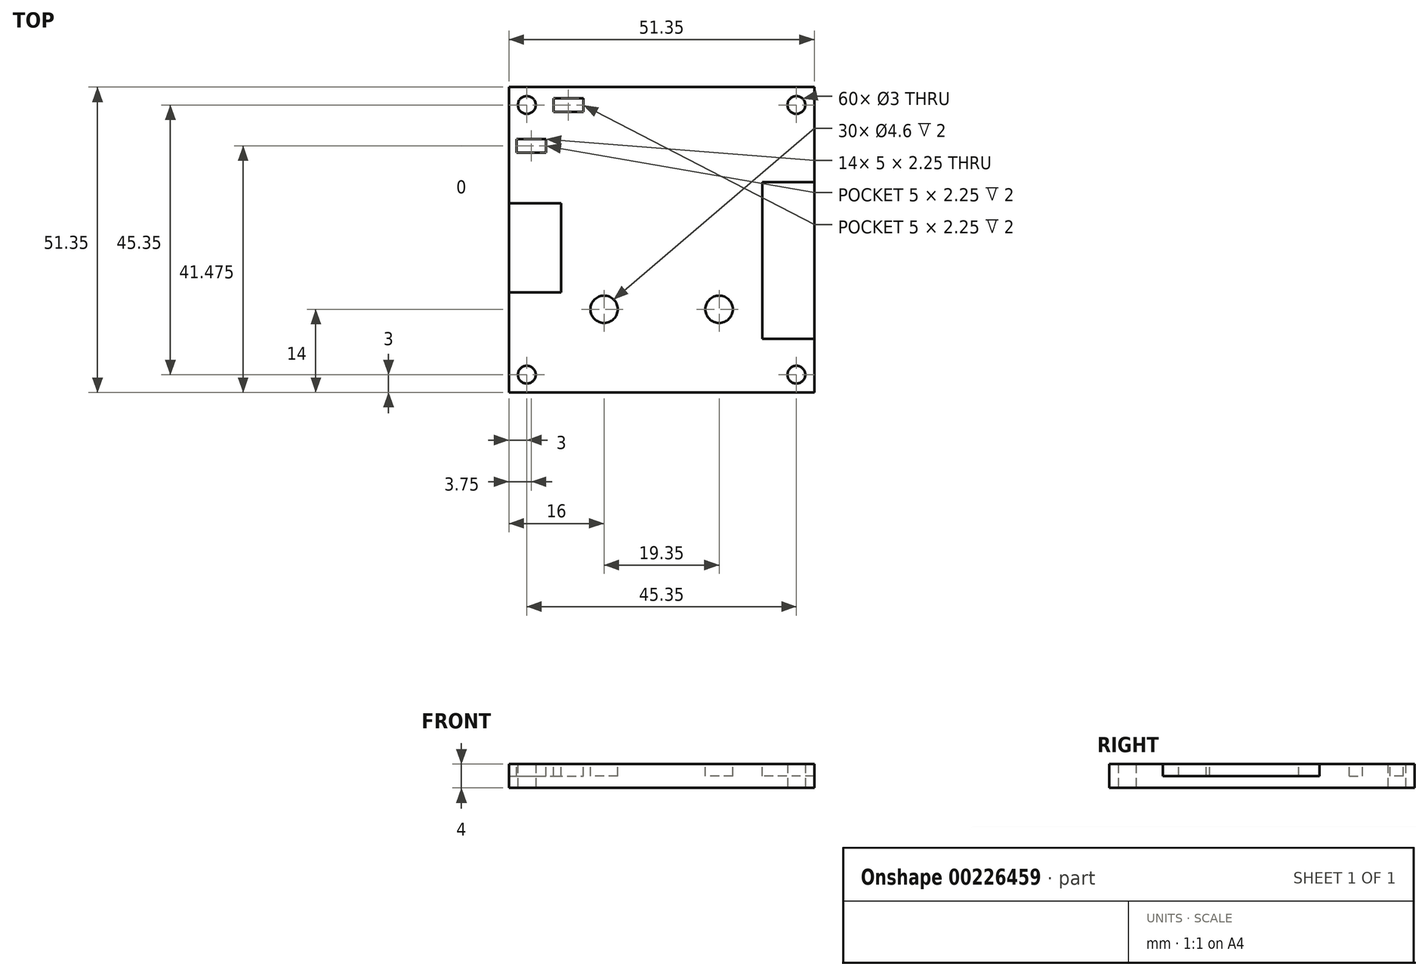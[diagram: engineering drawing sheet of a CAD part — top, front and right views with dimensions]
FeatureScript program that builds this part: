
annotation { "Feature Type Name" : "Feature", "Feature Type Description" : "" }
export const myFeature = defineFeature(function(context is Context, id is Id, definition is map)
    precondition{}
    {
        {
            var Q0;
            Q0=qCreatedBy(makeId("Top.planeOp"),FACE);
            var sketch = newSketch(context, id + "F0", { "sketchPlane" : qUnion([Q0])});
            skLineSegment(sketch, "E0.bottom", {"start": v(0, 0) * mm, "end": v(51.35, 0) * mm});
            skLineSegment(sketch, "E0.top", {"start": v(0, -51.35) * mm, "end": v(51.35, -51.35) * mm});
            skLineSegment(sketch, "E0.left", {"start": v(0, 0) * mm, "end": v(0, -51.35) * mm});
            skLineSegment(sketch, "E0.right", {"start": v(51.35, 0) * mm, "end": v(51.35, -51.35) * mm});
            skCircle(sketch, "E1", {"center": v(3, -3) * mm, "radius": 1.5 * mm});
            skCircle(sketch, "E2", {"center": v(48.35, -3) * mm, "radius": 1.5 * mm});
            skCircle(sketch, "E3", {"center": v(48.35, -48.35) * mm, "radius": 1.5 * mm});
            skCircle(sketch, "E4", {"center": v(3, -48.35) * mm, "radius": 1.5 * mm});
            skLineSegment(sketch, "E5", {"start": v(0, -3) * mm, "end": v(1.5, -3) * mm});
            skLineSegment(sketch, "E6", {"start": v(51.35, -3) * mm, "end": v(49.85, -3) * mm});
            skLineSegment(sketch, "E7", {"start": v(3, -1.5) * mm, "end": v(3, 0) * mm});
            skLineSegment(sketch, "E8", {"start": v(3, -51.35) * mm, "end": v(3, -48.35) * mm});
            skLineSegment(sketch, "E9", {"start": v(3, -48.35) * mm, "end": v(0, -48.35) * mm});
            skLineSegment(sketch, "E10", {"start": v(48.35, -48.35) * mm, "end": v(51.35, -48.35) * mm});
            skLineSegment(sketch, "E11", {"start": v(48.35, -48.35) * mm, "end": v(48.35, -51.35) * mm});
            skLineSegment(sketch, "E12", {"start": v(1.5, -3) * mm, "end": v(3, -3) * mm});
            skLineSegment(sketch, "E13", {"start": v(3, -3) * mm, "end": v(3, -1.5) * mm});
            skLineSegment(sketch, "E14", {"start": v(48.35, -3) * mm, "end": v(49.85, -3) * mm});
            skLineSegment(sketch, "E15", {"start": v(48.35, -3) * mm, "end": v(48.35, 0) * mm});
            skSolve(sketch);
        }
        {
            var Q0;
            {var subQ0=sQuery(id+"F0.wireOp",EDGE,"E5");Q0=makeQuery(id+"F0.imprint","IMPRINT",FACE,{"disambiguationData":[TD([[makeQuery(id+"F0.imprint","IMPRINT",EDGE,{"derivedFrom":subQ0}),-1.0]])]});}
            var Q1;
            {var subQ1=sQuery(id+"F0.wireOp",EDGE,"E0.top");var subQ7=sQuery(id+"F0.wireOp",EDGE,"E0.left");var subQ8=makeQuery(id+"F0.imprint","INTERSECT",VERTEX,{"derivedFrom":[subQ1,subQ7]});Q1=makeQuery(id+"F0.imprint","IMPRINT",FACE,{"disambiguationData":[TD([[makeQuery(id+"F0.imprint","IMPRINT",EDGE,{"disambiguationData":[TD([[subQ8,-1.0]])],"derivedFrom":subQ1}),1.0]])]});}
            var Q2;
            {var subQ1=sQuery(id+"F0.wireOp",EDGE,"E0.right");var subQ7=sQuery(id+"F0.wireOp",EDGE,"E0.top");var subQ8=makeQuery(id+"F0.imprint","INTERSECT",VERTEX,{"derivedFrom":[subQ7,subQ1]});Q2=makeQuery(id+"F0.imprint","IMPRINT",FACE,{"disambiguationData":[TD([[makeQuery(id+"F0.imprint","IMPRINT",EDGE,{"disambiguationData":[TD([[subQ8,1.0]])],"derivedFrom":subQ7}),1.0]])]});}
            var Q3;
            {var subQ0=sQuery(id+"F0.wireOp",EDGE,"E6");Q3=makeQuery(id+"F0.imprint","IMPRINT",FACE,{"disambiguationData":[TD([[makeQuery(id+"F0.imprint","IMPRINT",EDGE,{"derivedFrom":subQ0}),-1.0]])]});}
            var Q4;
            {var subQ0=sQuery(id+"F0.wireOp",EDGE,"E5");Q4=makeQuery(id+"F0.imprint","IMPRINT",FACE,{"disambiguationData":[TD([[makeQuery(id+"F0.imprint","IMPRINT",EDGE,{"derivedFrom":subQ0}),1.0]])]});}
            extrude(context, id + "F1", {"entities" : qUnion([Q0, Q1, Q2, Q3, Q4]), "depth" : 4 * mm});
        }
        {
            var Q0;
            Q0=makeQuery(id+"F1.opExtrude","CAP_FACE",FACE,{"disambiguationData":[OSD([sQuery(id+"F0.wireOp",EDGE,"E0.bottom"),sQuery(id+"F0.wireOp",EDGE,"E0.top"),sQuery(id+"F0.wireOp",EDGE,"E0.left"),sQuery(id+"F0.wireOp",EDGE,"E0.right"),sQuery(id+"F0.wireOp",EDGE,"E1"),sQuery(id+"F0.wireOp",EDGE,"E2"),sQuery(id+"F0.wireOp",EDGE,"E3"),sQuery(id+"F0.wireOp",EDGE,"E4")])],"isStart":false});
            var sketch = newSketch(context, id + "F2", { "sketchPlane" : qUnion([Q0])});
            skLineSegment(sketch, "E16", {"start": v(0, -6) * mm, "end": v(6, -6) * mm});
            skLineSegment(sketch, "E17", {"start": v(6, -6) * mm, "end": v(6, 0) * mm});
            skLineSegment(sketch, "E18", {"start": v(45.35, 0) * mm, "end": v(45.35, -6) * mm});
            skLineSegment(sketch, "E19", {"start": v(45.35, -6) * mm, "end": v(51.35, -6) * mm});
            skLineSegment(sketch, "E20", {"start": v(51.35, -45.35) * mm, "end": v(45.35, -45.35) * mm});
            skLineSegment(sketch, "E21", {"start": v(45.35, -45.35) * mm, "end": v(45.35, -51.35) * mm});
            skLineSegment(sketch, "E22", {"start": v(6, -51.35) * mm, "end": v(6, -45.35) * mm});
            skLineSegment(sketch, "E23", {"start": v(6, -45.35) * mm, "end": v(0, -45.35) * mm});
            skLineSegment(sketch, "E24", {"start": v(51.35, 0) * mm, "end": v(51.35, -16) * mm});
            skLineSegment(sketch, "E25", {"start": v(51.35, -51.35) * mm, "end": v(51.35, -42.35) * mm});
            skLineSegment(sketch, "E26.bottom", {"start": v(51.35, -16) * mm, "end": v(42.6, -16) * mm});
            skLineSegment(sketch, "E26.top", {"start": v(51.35, -42.35) * mm, "end": v(42.6, -42.35) * mm});
            skLineSegment(sketch, "E26.left", {"start": v(51.35, -16) * mm, "end": v(51.35, -42.35) * mm});
            skLineSegment(sketch, "E26.right", {"start": v(42.6, -16) * mm, "end": v(42.6, -42.35) * mm});
            skCircle(sketch, "E27", {"center": v(35.35, -37.35) * mm, "radius": 2.3 * mm});
            skCircle(sketch, "E28", {"center": v(16, -37.35) * mm, "radius": 2.3 * mm});
            skLineSegment(sketch, "E29", {"start": v(16, -37.35) * mm, "end": v(16, -51.35) * mm});
            skLineSegment(sketch, "E30", {"start": v(35.35, -37.35) * mm, "end": v(35.35, -51.35) * mm});
            skLineSegment(sketch, "E31", {"start": v(16, -37.35) * mm, "end": v(0, -37.35) * mm});
            skLineSegment(sketch, "E32", {"start": v(35.35, -37.35) * mm, "end": v(51.35, -37.35) * mm});
            skLineSegment(sketch, "E33.top", {"start": v(7.5, -4.15) * mm, "end": v(12.5, -4.15) * mm});
            skLineSegment(sketch, "E33.left", {"start": v(7.5, -1.9) * mm, "end": v(7.5, -4.15) * mm});
            skLineSegment(sketch, "E33.right", {"start": v(12.5, -1.9) * mm, "end": v(12.5, -4.15) * mm});
            skLineSegment(sketch, "E34", {"start": v(7.5, -1.9) * mm, "end": v(12.5, -1.9) * mm});
            skLineSegment(sketch, "E35.bottom", {"start": v(1.25, -11) * mm, "end": v(6.25, -11) * mm});
            skLineSegment(sketch, "E35.top", {"start": v(1.25, -8.75) * mm, "end": v(6.25, -8.75) * mm});
            skLineSegment(sketch, "E35.left", {"start": v(1.25, -11) * mm, "end": v(1.25, -8.75) * mm});
            skLineSegment(sketch, "E35.right", {"start": v(6.25, -11) * mm, "end": v(6.25, -8.75) * mm});
            skLineSegment(sketch, "E36.bottom", {"start": v(0, -19.5) * mm, "end": v(8.75, -19.5) * mm});
            skLineSegment(sketch, "E36.top", {"start": v(0, -34.5) * mm, "end": v(8.75, -34.5) * mm});
            skLineSegment(sketch, "E36.left", {"start": v(0, -19.5) * mm, "end": v(0, -34.5) * mm});
            skLineSegment(sketch, "E36.right", {"start": v(8.75, -19.5) * mm, "end": v(8.75, -34.5) * mm});
            skSolve(sketch);
        }
        {
            var Q0;
            Q0=makeQuery(id+"F2.imprint","IMPRINT",FACE,{"disambiguationData":[TD([[makeQuery(id+"F2.imprint","IMPRINT",EDGE,{"derivedFrom":sQuery(id+"F2.wireOp",EDGE,"E35.bottom")}),1.0]])]});
            var Q1;
            Q1=makeQuery(id+"F2.imprint","IMPRINT",FACE,{"disambiguationData":[TD([[makeQuery(id+"F2.imprint","IMPRINT",EDGE,{"derivedFrom":sQuery(id+"F2.wireOp",EDGE,"E36.bottom")}),-1.0]])]});
            var Q2;
            {var subQ0=sQuery(id+"F2.wireOp",EDGE,"E29");var subQ1=sQuery(id+"F2.wireOp",EDGE,"E28");var subQ2=makeQuery(id+"F2.imprint","INTERSECT",VERTEX,{"derivedFrom":[subQ1,subQ0]});Q2=makeQuery(id+"F2.imprint","IMPRINT",FACE,{"disambiguationData":[TD([[makeQuery(id+"F2.imprint","IMPRINT",EDGE,{"disambiguationData":[TD([[subQ2,-1.0]])],"derivedFrom":subQ1}),1.0]])]});}
            var Q3;
            {var subQ0=sQuery(id+"F2.wireOp",EDGE,"E29");var subQ1=sQuery(id+"F2.wireOp",EDGE,"E28");var subQ2=makeQuery(id+"F2.imprint","INTERSECT",VERTEX,{"derivedFrom":[subQ1,subQ0]});Q3=makeQuery(id+"F2.imprint","IMPRINT",FACE,{"disambiguationData":[TD([[makeQuery(id+"F2.imprint","IMPRINT",EDGE,{"disambiguationData":[TD([[subQ2,1.0]])],"derivedFrom":subQ1}),1.0]])]});}
            var Q4;
            {var subQ0=sQuery(id+"F2.wireOp",EDGE,"E30");var subQ1=sQuery(id+"F2.wireOp",EDGE,"E27");var subQ2=makeQuery(id+"F2.imprint","INTERSECT",VERTEX,{"derivedFrom":[subQ1,subQ0]});Q4=makeQuery(id+"F2.imprint","IMPRINT",FACE,{"disambiguationData":[TD([[makeQuery(id+"F2.imprint","IMPRINT",EDGE,{"disambiguationData":[TD([[subQ2,-1.0]])],"derivedFrom":subQ1}),1.0]])]});}
            var Q5;
            {var subQ0=sQuery(id+"F2.wireOp",EDGE,"E30");var subQ1=sQuery(id+"F2.wireOp",EDGE,"E27");var subQ2=makeQuery(id+"F2.imprint","INTERSECT",VERTEX,{"derivedFrom":[subQ1,subQ0]});Q5=makeQuery(id+"F2.imprint","IMPRINT",FACE,{"disambiguationData":[TD([[makeQuery(id+"F2.imprint","IMPRINT",EDGE,{"disambiguationData":[TD([[subQ2,1.0]])],"derivedFrom":subQ1}),1.0]])]});}
            var Q6;
            {var subQ0=sQuery(id+"F2.wireOp",EDGE,"E26.bottom");Q6=makeQuery(id+"F2.imprint","IMPRINT",FACE,{"disambiguationData":[TD([[makeQuery(id+"F2.imprint","IMPRINT",EDGE,{"derivedFrom":subQ0}),1.0]])]});}
            var Q7;
            {var subQ0=sQuery(id+"F2.wireOp",EDGE,"E26.top");Q7=makeQuery(id+"F2.imprint","IMPRINT",FACE,{"disambiguationData":[TD([[makeQuery(id+"F2.imprint","IMPRINT",EDGE,{"derivedFrom":subQ0}),-1.0]])]});}
            var Q8;
            Q8=makeQuery(id+"F2.imprint","IMPRINT",FACE,{"disambiguationData":[TD([[makeQuery(id+"F2.imprint","IMPRINT",EDGE,{"derivedFrom":sQuery(id+"F2.wireOp",EDGE,"E33.top")}),1.0]])]});
            extrude(context, id + "F3", {"entities" : qUnion([Q0, Q1, Q2, Q3, Q4, Q5, Q6, Q7, Q8]), "operationType" : NewBodyOperationType.REMOVE, "oppositeDirection" : true, "depth" : 2 * mm});
        }
    });
